# Revit family: 10485 Велопарковка с навесом Velo-9 Хоббика
name_source: partatom
category: Антураж
revit_build: Autodesk Revit 2018 (Build: 20180423_1000(x64)
units: mm (PartAtom-declared; Revit-internal decimal feet)

## family parameters
Всегда вертикально = Да
Источник визуального образа = Геометрия семейства
На основе рабочей плоскости = Нет
Общий = Нет
При загрузке вырезать с полостями = Нет
Точка расчета площади = Нет

## types (5) — shared parameters
URL = https://hobbyka.ru
Артикул товара = Арт. 10485
Высота = 2352 мм
Группа модели = Велопарковки
Изготовитель = ООО «Хоббика»
Материал изделия = Сталь, поликарбонат
Цвет каркаса = Сталь
Цвет навеса = Крыша
Ширина = 1600 мм

## per-type parameters (varying)
| type | 10 мест | 15 мест | 19 мест | 30 мест | 5 мест | Длина | Кол-во опор | Кол-во стоек | Описание |
| 5 мест | Нет | Нет | Нет | Нет | Да | 1140 мм | 3 | 6 | Велопарковка с навесом Velo-9. Версия на 5 мест |
| 10 мест | Да | Нет | Нет | Нет | Нет | 2240 мм | 4 | 11 | Велопарковка с навесом Velo-9. Версия на 10 мест |
| 15 мест | Нет | Да | Нет | Нет | Нет | 3340 мм | 5 | 16 | Велопарковка с навесом Velo-9. Версия на 15 мест |
| 19 мест | Нет | Нет | Да | Нет | Нет | 4220 мм | 6 | 20 | Велопарковка с навесом Velo-9. Версия на 19 мест |
| 30 мест | Нет | Нет | Нет | Да | Нет | 6638 мм | 8 | 31 | Велопарковка с навесом Velo-9. Версия на 30 мест |
